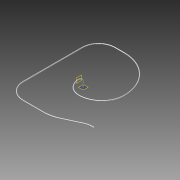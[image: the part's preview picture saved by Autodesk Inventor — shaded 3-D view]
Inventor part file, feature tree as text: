
AUTODESK INVENTOR PART (.ipt)
format: ipt  version: 2015 (Build 190159000, 159)  size: 162,304 bytes
history: native  units: mm
features: plane x2, sweep x1, sketch x1
ambient origin geometry x8: Origin, YZ Plane, XZ Plane, XY Plane, X Axis, Y Axis, Z Axis, Center Point
bodies: Solid1 (feature_tree)
feature tree (4):
  plane  "Plano de trabajo2"
  plane  "Plano de trabajo3"
  sweep  "Barrido2"
  sketch  "Boceto 3D1"  dims[d9=3.0mm d10=40.0mm d12=24.0mm d14=64.0mm d15=104.0mm d16=168.0mm d17=272.0mm d18=55.0mm d19=175.0mm d20=150.0mm d21=75.0mm d24=75.0mm d25=4.363323mm d27=343.0mm d28=365.0mm d29=225.0mm d30=75.0mm d35=22.0mm d36=4.0mm d37=3.0mm d38=20.0mm d39=0.0mm d40=0.0mm]
